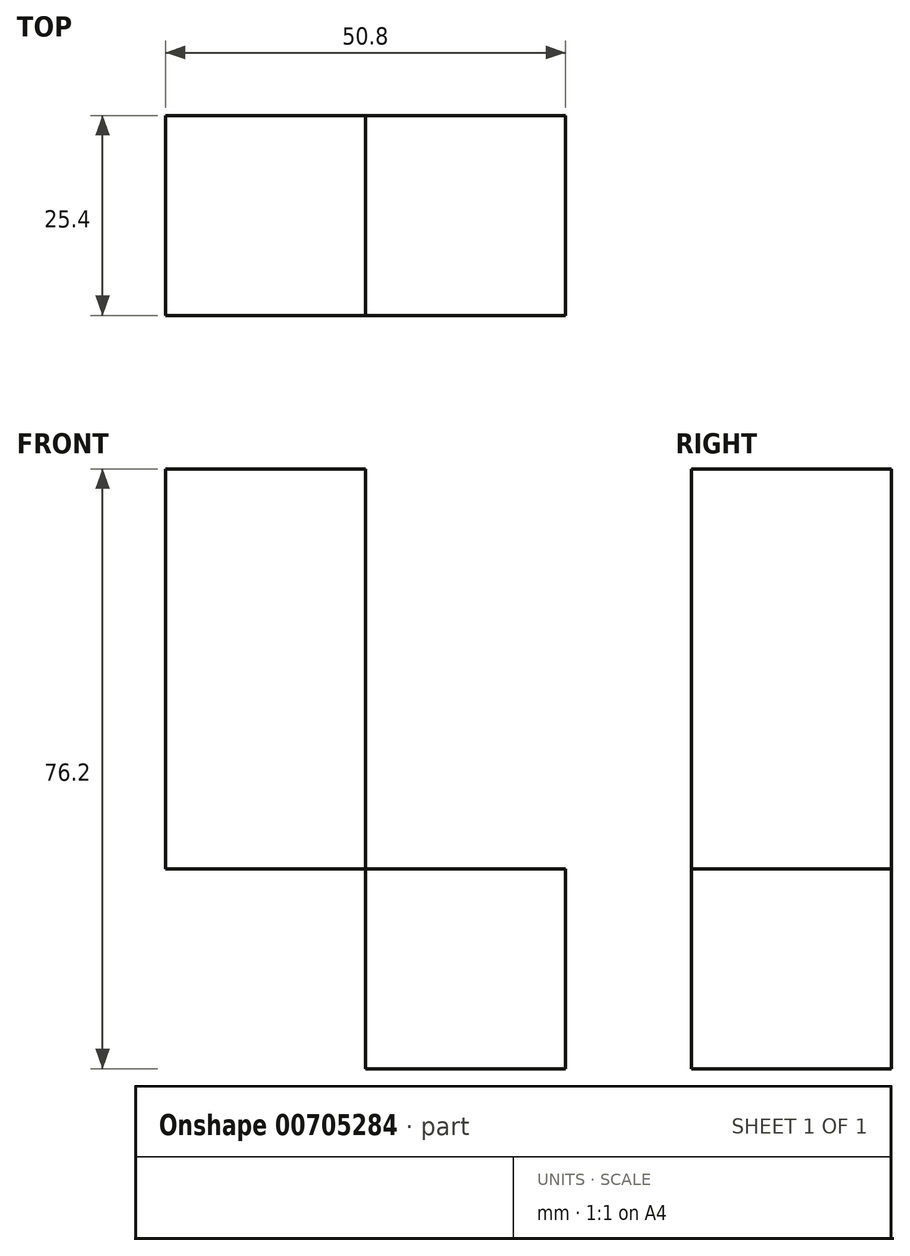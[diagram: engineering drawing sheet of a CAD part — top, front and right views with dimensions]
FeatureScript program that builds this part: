
annotation { "Feature Type Name" : "Feature", "Feature Type Description" : "" }
export const myFeature = defineFeature(function(context is Context, id is Id, definition is map)
    precondition{}
    {
        {
            var Q0;
            Q0=qCreatedBy(makeId("Front.planeOp"),FACE);
            var sketch = newSketch(context, id + "F0", { "sketchPlane" : qUnion([Q0])});
            skLineSegment(sketch, "E0.bottom", {"start": v(0, 0) * mm, "end": v(-25.4, 0) * mm});
            skLineSegment(sketch, "E0.top", {"start": v(0, 25.4) * mm, "end": v(-25.4, 25.4) * mm});
            skLineSegment(sketch, "E0.left", {"start": v(0, 0) * mm, "end": v(0, 25.4) * mm});
            skLineSegment(sketch, "E0.right", {"start": v(-25.4, 0) * mm, "end": v(-25.4, 25.4) * mm});
            skLineSegment(sketch, "E1.top", {"start": v(0, 50.8) * mm, "end": v(-25.4, 50.8) * mm});
            skLineSegment(sketch, "E1.left", {"start": v(0, 25.4) * mm, "end": v(0, 50.8) * mm});
            skLineSegment(sketch, "E1.right", {"start": v(-25.4, 25.4) * mm, "end": v(-25.4, 50.8) * mm});
            skLineSegment(sketch, "E2.bottom", {"start": v(-25.4, 0) * mm, "end": v(0, 0) * mm});
            skLineSegment(sketch, "E2.top", {"start": v(-25.4, -25.4) * mm, "end": v(0, -25.4) * mm});
            skLineSegment(sketch, "E2.left", {"start": v(-25.4, 0) * mm, "end": v(-25.4, -25.4) * mm});
            skLineSegment(sketch, "E2.right", {"start": v(0, 0) * mm, "end": v(0, -25.4) * mm});
            skLineSegment(sketch, "E3.bottom", {"start": v(0, -25.4) * mm, "end": v(25.4, -25.4) * mm});
            skLineSegment(sketch, "E3.top", {"start": v(0, 0) * mm, "end": v(25.4, 0) * mm});
            skLineSegment(sketch, "E3.left", {"start": v(0, -25.4) * mm, "end": v(0, 0) * mm});
            skLineSegment(sketch, "E3.right", {"start": v(25.4, -25.4) * mm, "end": v(25.4, 0) * mm});
            skSolve(sketch);
        }
        {
            var Q0;
            Q0=makeQuery(id+"F0.imprint","IMPRINT",FACE,{"disambiguationData":[TD([[makeQuery(id+"F0.imprint","IMPRINT",EDGE,{"derivedFrom":sQuery(id+"F0.wireOp",EDGE,"E3.bottom")}),1.0]])]});
            var Q1;
            Q1=makeQuery(id+"F0.imprint","IMPRINT",FACE,{"disambiguationData":[TD([[makeQuery(id+"F0.imprint","IMPRINT",EDGE,{"derivedFrom":sQuery(id+"F0.wireOp",EDGE,"E0.left")}),1.0]])]});
            var Q2;
            Q2=makeQuery(id+"F0.imprint","IMPRINT",FACE,{"disambiguationData":[TD([[makeQuery(id+"F0.imprint","IMPRINT",EDGE,{"derivedFrom":sQuery(id+"F0.wireOp",EDGE,"E2.bottom")}),-1.0]])]});
            var Q3;
            Q3=makeQuery(id+"F0.imprint","IMPRINT",FACE,{"disambiguationData":[TD([[makeQuery(id+"F0.imprint","IMPRINT",EDGE,{"derivedFrom":sQuery(id+"F0.wireOp",EDGE,"E0.top")}),-1.0]])]});
            extrude(context, id + "F1", {"entities" : qUnion([Q0, Q1, Q2, Q3]), "depth" : 25.4 * mm, "offsetDistance" : 25.4 * mm});
        }
    });
